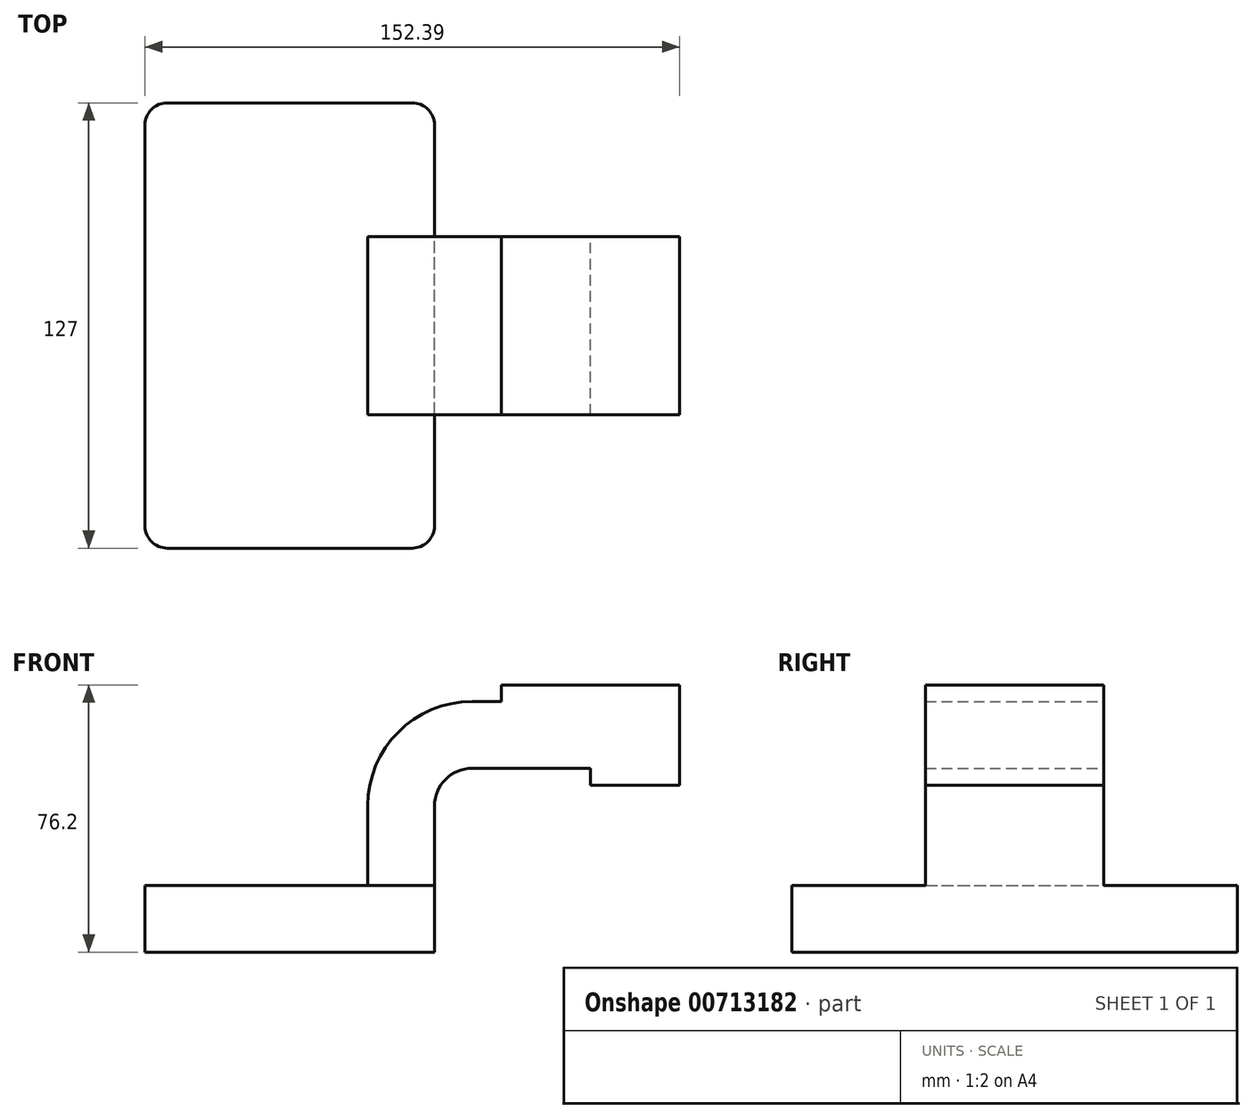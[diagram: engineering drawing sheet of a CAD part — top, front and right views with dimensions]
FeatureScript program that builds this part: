
annotation { "Feature Type Name" : "Feature", "Feature Type Description" : "" }
export const myFeature = defineFeature(function(context is Context, id is Id, definition is map)
    precondition{}
    {
        {
            var Q0;
            Q0=qCreatedBy(makeId("Front.planeOp"),FACE);
            var sketch = newSketch(context, id + "F0", { "sketchPlane" : qUnion([Q0])});
            skLineSegment(sketch, "E0.bottom", {"start": v(-41.28, 9.52) * mm, "end": v(41.27, 9.53) * mm});
            skLineSegment(sketch, "E0.top", {"start": v(-41.28, -9.53) * mm, "end": v(41.28, -9.53) * mm});
            skLineSegment(sketch, "E0.left", {"start": v(-41.28, 9.52) * mm, "end": v(-41.27, -9.53) * mm});
            skLineSegment(sketch, "E0.right", {"start": v(41.28, 9.53) * mm, "end": v(41.28, -9.52) * mm});
            skPoint(sketch, "E0.middle", {"position": v(0, 0) * mm});
            skLineSegment(sketch, "E1.bottom", {"start": v(60.33, 66.67) * mm, "end": v(111.12, 66.67) * mm});
            skLineSegment(sketch, "E1.top", {"start": v(60.33, 38.1) * mm, "end": v(111.12, 38.1) * mm});
            skLineSegment(sketch, "E1.left", {"start": v(60.33, 66.67) * mm, "end": v(60.32, 38.1) * mm});
            skLineSegment(sketch, "E1.right", {"start": v(111.13, 66.67) * mm, "end": v(111.12, 38.1) * mm});
            skPoint(sketch, "E1.middle", {"position": v(85.72, 52.39) * mm});
            skLineSegment(sketch, "E2", {"start": v(41.27, 9.53) * mm, "end": v(41.27, 32.18) * mm});
            skArc(sketch, "E3", {"start": v(41.27, 32.18) * mm, "mid": v(44.4, 39.74) * mm, "end": v(51.97, 42.88) * mm});
            skLineSegment(sketch, "E4", {"start": v(51.97, 42.88) * mm, "end": v(85.72, 42.88) * mm});
            skLineSegment(sketch, "E5.0", {"start": v(51.97, 61.93) * mm, "end": v(77.24, 61.93) * mm});
            skArc(sketch, "E5.1", {"start": v(22.22, 32.18) * mm, "mid": v(30.94, 53.21) * mm, "end": v(51.97, 61.93) * mm});
            skLineSegment(sketch, "E5.2", {"start": v(22.22, 9.53) * mm, "end": v(22.22, 32.18) * mm});
            skFitSpline(sketch, "E6", {"points": [v(-41.28, 9.53) * mm, v(51.97, 61.93) * mm], "startDerivative": vector(72.3, 81.5) * mm, "endDerivative": vector(113.81, -7.05) * mm});
            skLineSegment(sketch, "E7", {"start": v(85.72, 38.1) * mm, "end": v(85.72, 66.67) * mm});
            skSolve(sketch);
        }
        {
            var Q0;
            Q0=makeQuery(id+"F0.imprint","IMPRINT",FACE,{"disambiguationData":[TD([[makeQuery(id+"F0.imprint","IMPRINT",EDGE,{"derivedFrom":sQuery(id+"F0.wireOp",EDGE,"E0.top")}),1.0]])]});
            extrude(context, id + "F1", {"entities" : qUnion([Q0]), "endBound" : BoundingType.SYMMETRIC, "depth" : 127 * mm, "offsetDistance" : 25.4 * mm});
        }
        {
            var Q0;
            {var subQ1=sQuery(id+"F0.wireOp",EDGE,"E2");Q0=makeQuery(id+"F0.imprint","IMPRINT",FACE,{"disambiguationData":[TD([[makeQuery(id+"F0.imprint","IMPRINT",EDGE,{"derivedFrom":subQ1}),1.0]])]});}
            var Q1;
            {var subQ3=sQuery(id+"F0.wireOp",EDGE,"E1.left");var subQ5=sQuery(id+"F0.wireOp",EDGE,"E1.bottom");var subQ6=makeQuery(id+"F0.imprint","INTERSECT",VERTEX,{"derivedFrom":[subQ5,subQ3]});Q1=makeQuery(id+"F0.imprint","IMPRINT",FACE,{"disambiguationData":[TD([[makeQuery(id+"F0.imprint","IMPRINT",EDGE,{"disambiguationData":[TD([[subQ6,-1.0]])],"derivedFrom":subQ5}),-1.0]])]});}
            extrude(context, id + "F2", {"entities" : qUnion([Q0, Q1]), "operationType" : NewBodyOperationType.ADD, "endBound" : BoundingType.SYMMETRIC, "depth" : 50.8 * mm, "offsetDistance" : 25.4 * mm});
        }
        {
            var Q0;
            Q0=makeQuery(id+"F0.imprint","IMPRINT",FACE,{"disambiguationData":[TD([[makeQuery(id+"F0.imprint","IMPRINT",EDGE,{"derivedFrom":sQuery(id+"F0.wireOp",EDGE,"E5.1")}),1.0]])]});
            extrude(context, id + "F3", {"entities" : qUnion([Q0]), "operationType" : NewBodyOperationType.ADD, "endBound" : BoundingType.SYMMETRIC, "depth" : 15.88 * mm, "offsetDistance" : 25.4 * mm});
        }
        {
            var Q0;
            {var subQ0=sQuery(id+"F0.wireOp",EDGE,"E1.right");Q0=makeQuery(id+"F0.imprint","IMPRINT",FACE,{"disambiguationData":[TD([[makeQuery(id+"F0.imprint","IMPRINT",EDGE,{"derivedFrom":subQ0}),-1.0]])]});}
            extrude(context, id + "F4", {"entities" : qUnion([Q0]), "operationType" : NewBodyOperationType.ADD, "endBound" : BoundingType.SYMMETRIC, "depth" : 50.8 * mm, "offsetDistance" : 25.4 * mm});
        }
        {
            var Q0;
            Q0=makeQuery(id+"F1.opExtrude","CAP_EDGE",EDGE,{"disambiguationData":[OSD([sQuery(id+"F0.wireOp",EDGE,"E0.left")])],"isStart":false});
            var Q1;
            Q1=makeQuery(id+"F1.opExtrude","CAP_EDGE",EDGE,{"disambiguationData":[OSD([sQuery(id+"F0.wireOp",EDGE,"E0.right")])],"isStart":false});
            var Q2;
            Q2=makeQuery(id+"F1.opExtrude","CAP_EDGE",EDGE,{"disambiguationData":[OSD([sQuery(id+"F0.wireOp",EDGE,"E0.left")])],"isStart":true});
            var Q3;
            Q3=makeQuery(id+"F1.opExtrude","CAP_EDGE",EDGE,{"disambiguationData":[OSD([sQuery(id+"F0.wireOp",EDGE,"E0.right")])],"isStart":true});
            fillet(context, id + "F5", {"entities" : qUnion([Q0, Q1, Q2, Q3]), "radius" : 6.35 * mm, "tangentPropagation" : true, "allowEdgeOverflow" : false});
        }
    });
